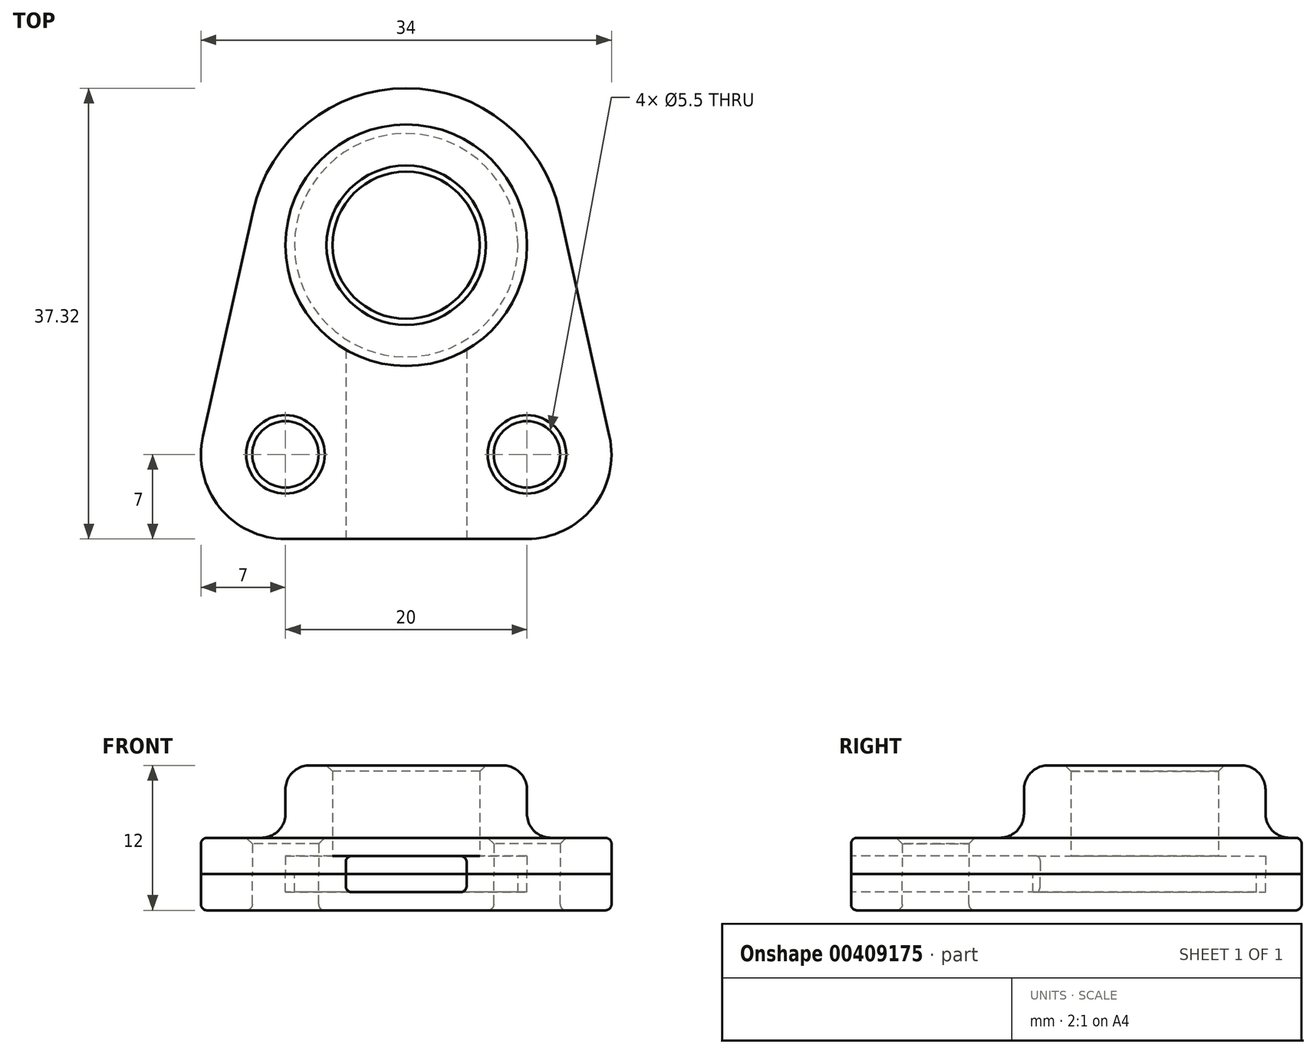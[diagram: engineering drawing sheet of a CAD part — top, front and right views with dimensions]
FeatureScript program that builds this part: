
annotation { "Feature Type Name" : "Feature", "Feature Type Description" : "" }
export const myFeature = defineFeature(function(context is Context, id is Id, definition is map)
    precondition{}
    {
        {
            var Q0;
            Q0=qCreatedBy(makeId("Top.planeOp"),FACE);
            var sketch = newSketch(context, id + "F0", { "sketchPlane" : qUnion([Q0])});
            skCircle(sketch, "E0", {"center": v(-20, 0) * mm, "radius": 2.75 * mm});
            skCircle(sketch, "E1", {"center": v(-10, 17.32) * mm, "radius": 10 * mm});
            skCircle(sketch, "E2", {"center": v(-10, 17.32) * mm, "radius": 6.1 * mm});
            skCircle(sketch, "E3", {"center": v(-10, 17.32) * mm, "radius": 5 * mm});
            skCircle(sketch, "E4", {"center": v(0, 0) * mm, "radius": 2.75 * mm});
            skLineSegment(sketch, "E5", {"start": v(-20, 0) * mm, "end": v(-10, 17.32) * mm, "construction": true});
            skLineSegment(sketch, "E6", {"start": v(-10, 17.32) * mm, "end": v(0, 0) * mm, "construction": true});
            skLineSegment(sketch, "E7", {"start": v(-20, 0) * mm, "end": v(0, 0) * mm, "construction": true});
            skArc(sketch, "E8", {"start": v(-26.83, 1.52) * mm, "mid": v(-25.46, -4.38) * mm, "end": v(-20, -7) * mm});
            skLineSegment(sketch, "E9", {"start": v(-27, 15.14) * mm, "end": v(-27, -13) * mm, "construction": true});
            skLineSegment(sketch, "E10", {"start": v(-10, 17.32) * mm, "end": v(-10, 0) * mm, "construction": true});
            skArc(sketch, "E11", {"start": v(2.69, 20.14) * mm, "mid": v(-10, 30.32) * mm, "end": v(-22.69, 20.14) * mm});
            skLineSegment(sketch, "E12", {"start": v(-22.69, 20.14) * mm, "end": v(-26.83, 1.52) * mm});
            skArc(sketch, "E13.MirrorC", {"start": v(6.83, 1.52) * mm, "mid": v(5.46, -4.38) * mm, "end": v(0, -7) * mm});
            skLineSegment(sketch, "E14.MirrorCS", {"start": v(2.69, 20.14) * mm, "end": v(6.83, 1.52) * mm});
            skLineSegment(sketch, "E15", {"start": v(-20, -7) * mm, "end": v(0, -7) * mm});
            skLineSegment(sketch, "E16", {"start": v(-15, 8.66) * mm, "end": v(-15, -7) * mm});
            skLineSegment(sketch, "E17.MirrorCS", {"start": v(-5, 8.66) * mm, "end": v(-5, -7) * mm});
            skCircle(sketch, "E18", {"center": v(-10, 17.32) * mm, "radius": 9.25 * mm});
            skSolve(sketch);
        }
        {
            var Q0;
            Q0=makeQuery(id+"F0.imprint","IMPRINT",FACE,{"disambiguationData":[TD([[makeQuery(id+"F0.imprint","IMPRINT",EDGE,{"derivedFrom":sQuery(id+"F0.wireOp",EDGE,"E0")}),-1.0]])]});
            var Q1;
            Q1=makeQuery(id+"F0.imprint","IMPRINT",FACE,{"disambiguationData":[TD([[makeQuery(id+"F0.imprint","IMPRINT",EDGE,{"derivedFrom":sQuery(id+"F0.wireOp",EDGE,"E1")}),1.0]])]});
            var Q2;
            {var subQ0=sQuery(id+"F0.wireOp",EDGE,"E16");Q2=makeQuery(id+"F0.imprint","IMPRINT",FACE,{"disambiguationData":[TD([[makeQuery(id+"F0.imprint","IMPRINT",EDGE,{"derivedFrom":subQ0}),1.0]])]});}
            extrude(context, id + "F1", {"entities" : qUnion([Q0, Q1, Q2]), "depth" : 3 * mm, "offsetDistance" : 25 * mm});
        }
        {
            var Q0;
            Q0=makeQuery(id+"F0.imprint","IMPRINT",FACE,{"disambiguationData":[TD([[makeQuery(id+"F0.imprint","IMPRINT",EDGE,{"derivedFrom":sQuery(id+"F0.wireOp",EDGE,"E1")}),1.0]])]});
            var Q1;
            Q1=makeQuery(id+"F0.imprint","IMPRINT",FACE,{"disambiguationData":[TD([[makeQuery(id+"F0.imprint","IMPRINT",EDGE,{"derivedFrom":sQuery(id+"F0.wireOp",EDGE,"E2")}),-1.0]])]});
            extrude(context, id + "F2", {"entities" : qUnion([Q0, Q1]), "operationType" : NewBodyOperationType.ADD, "depth" : 9 * mm});
        }
        {
            var Q0;
            Q0=makeQuery(id+"F0.imprint","IMPRINT",FACE,{"disambiguationData":[TD([[makeQuery(id+"F0.imprint","IMPRINT",EDGE,{"derivedFrom":sQuery(id+"F0.wireOp",EDGE,"E2")}),-1.0]])]});
            var Q1;
            {var subQ0=sQuery(id+"F0.wireOp",EDGE,"E16");Q1=makeQuery(id+"F0.imprint","IMPRINT",FACE,{"disambiguationData":[TD([[makeQuery(id+"F0.imprint","IMPRINT",EDGE,{"derivedFrom":subQ0}),1.0]])]});}
            var Q2;
            Q2=makeQuery(id+"F0.imprint","IMPRINT",FACE,{"disambiguationData":[TD([[makeQuery(id+"F0.imprint","IMPRINT",EDGE,{"derivedFrom":sQuery(id+"F0.wireOp",EDGE,"E18")}),-1.0]])]});
            extrude(context, id + "F3", {"entities" : qUnion([Q0, Q1, Q2]), "operationType" : NewBodyOperationType.REMOVE, "depth" : 1.5 * mm, "offsetDistance" : 25 * mm});
        }
        {
            var Q0;
            Q0=makeQuery(id+"F2.boolean.opBoolean","INTERSECT",EDGE,{"derivedFrom":[makeQuery(id+"F1.opExtrude","CAP_FACE",FACE,{"disambiguationData":[OSD([sQuery(id+"F0.wireOp",EDGE,"E0"),sQuery(id+"F0.wireOp",EDGE,"E2"),sQuery(id+"F0.wireOp",EDGE,"E4"),sQuery(id+"F0.wireOp",EDGE,"E8"),sQuery(id+"F0.wireOp",EDGE,"E11"),sQuery(id+"F0.wireOp",EDGE,"E12"),sQuery(id+"F0.wireOp",EDGE,"E13.MirrorC"),sQuery(id+"F0.wireOp",EDGE,"E14.MirrorCS"),sQuery(id+"F0.wireOp",EDGE,"E15")])],"isStart":false}),makeQuery(id+"F2.opExtrude","SWEPT_FACE",FACE,{"disambiguationData":[OSD([sQuery(id+"F0.wireOp",EDGE,"E1")])]})]});
            var Q1;
            Q1=makeQuery(id+"F2.opExtrude","CAP_EDGE",EDGE,{"disambiguationData":[OSD([sQuery(id+"F0.wireOp",EDGE,"E1")])],"isStart":false});
            fillet(context, id + "F4", {"entities" : qUnion([Q0, Q1]), "radius" : 2 * mm, "tangentPropagation" : true, "allowEdgeOverflow" : false});
        }
        {
            var Q0;
            Q0=makeQuery(id+"F2.opExtrude","CAP_EDGE",EDGE,{"disambiguationData":[OSD([sQuery(id+"F0.wireOp",EDGE,"E2")])],"isStart":false});
            var Q1;
            Q1=makeQuery(id+"F1.opExtrude","CAP_EDGE",EDGE,{"disambiguationData":[OSD([sQuery(id+"F0.wireOp",EDGE,"E0")])],"isStart":false});
            var Q2;
            Q2=makeQuery(id+"F1.opExtrude","CAP_EDGE",EDGE,{"disambiguationData":[OSD([sQuery(id+"F0.wireOp",EDGE,"E4")])],"isStart":false});
            chamfer(context, id + "F5", {"entities" : qUnion([Q0, Q1, Q2]), "width" : 0.5 * mm, "tangentPropagation" : true});
        }
        {
            var Q0;
            Q0=makeQuery(id+"F0.imprint","IMPRINT",FACE,{"disambiguationData":[TD([[makeQuery(id+"F0.imprint","IMPRINT",EDGE,{"derivedFrom":sQuery(id+"F0.wireOp",EDGE,"E0")}),-1.0]])]});
            var Q1;
            {var subQ0=sQuery(id+"F0.wireOp",EDGE,"E16");Q1=makeQuery(id+"F0.imprint","IMPRINT",FACE,{"disambiguationData":[TD([[makeQuery(id+"F0.imprint","IMPRINT",EDGE,{"derivedFrom":subQ0}),1.0]])]});}
            var Q2;
            Q2=makeQuery(id+"F0.imprint","IMPRINT",FACE,{"disambiguationData":[TD([[makeQuery(id+"F0.imprint","IMPRINT",EDGE,{"derivedFrom":sQuery(id+"F0.wireOp",EDGE,"E2")}),-1.0]])]});
            var Q3;
            Q3=makeQuery(id+"F0.imprint","IMPRINT",FACE,{"disambiguationData":[TD([[makeQuery(id+"F0.imprint","IMPRINT",EDGE,{"derivedFrom":sQuery(id+"F0.wireOp",EDGE,"E3")}),1.0]])]});
            var Q4;
            Q4=makeQuery(id+"F0.imprint","IMPRINT",FACE,{"disambiguationData":[TD([[makeQuery(id+"F0.imprint","IMPRINT",EDGE,{"derivedFrom":sQuery(id+"F0.wireOp",EDGE,"E2")}),1.0]])]});
            var Q5;
            Q5=makeQuery(id+"F0.imprint","IMPRINT",FACE,{"disambiguationData":[TD([[makeQuery(id+"F0.imprint","IMPRINT",EDGE,{"derivedFrom":sQuery(id+"F0.wireOp",EDGE,"E18")}),-1.0]])]});
            extrude(context, id + "F6", {"entities" : qUnion([Q0, Q1, Q2, Q3, Q4, Q5]), "oppositeDirection" : true, "depth" : 3 * mm, "offsetDistance" : 25 * mm});
        }
        {
            var Q0;
            {var subQ0=sQuery(id+"F0.wireOp",EDGE,"E16");Q0=makeQuery(id+"F0.imprint","IMPRINT",FACE,{"disambiguationData":[TD([[makeQuery(id+"F0.imprint","IMPRINT",EDGE,{"derivedFrom":subQ0}),1.0]])]});}
            var Q1;
            Q1=makeQuery(id+"F0.imprint","IMPRINT",FACE,{"disambiguationData":[TD([[makeQuery(id+"F0.imprint","IMPRINT",EDGE,{"derivedFrom":sQuery(id+"F0.wireOp",EDGE,"E18")}),-1.0]])]});
            extrude(context, id + "F7", {"entities" : qUnion([Q0, Q1]), "operationType" : NewBodyOperationType.REMOVE, "oppositeDirection" : true, "depth" : 1.5 * mm, "offsetDistance" : 25 * mm});
        }
        {
            var Q0;
            Q0=makeQuery(id+"F6.opExtrude","CAP_FACE",FACE,{"disambiguationData":[OSD([sQuery(id+"F0.wireOp",EDGE,"E0"),sQuery(id+"F0.wireOp",EDGE,"E4"),sQuery(id+"F0.wireOp",EDGE,"E8"),sQuery(id+"F0.wireOp",EDGE,"E11"),sQuery(id+"F0.wireOp",EDGE,"E12"),sQuery(id+"F0.wireOp",EDGE,"E13.MirrorC"),sQuery(id+"F0.wireOp",EDGE,"E14.MirrorCS"),sQuery(id+"F0.wireOp",EDGE,"E15")])],"isStart":false});
            var Q1;
            Q1=makeQuery(id+"F7.boolean.opBoolean","COPY",EDGE,{"derivedFrom":makeQuery(id+"F7.opExtrude","CAP_EDGE",EDGE,{"disambiguationData":[OSD([sQuery(id+"F0.wireOp",EDGE,"E16")])],"isStart":false})});
            var Q2;
            Q2=makeQuery(id+"F7.boolean.opBoolean","COPY",EDGE,{"derivedFrom":makeQuery(id+"F7.opExtrude","CAP_EDGE",EDGE,{"disambiguationData":[OSD([sQuery(id+"F0.wireOp",EDGE,"E17.MirrorCS")])],"isStart":false})});
            var Q3;
            Q3=makeQuery(id+"F3.boolean.opBoolean","COPY",EDGE,{"derivedFrom":makeQuery(id+"F3.opExtrude","CAP_EDGE",EDGE,{"disambiguationData":[OSD([sQuery(id+"F0.wireOp",EDGE,"E17.MirrorCS")])],"isStart":false})});
            var Q4;
            Q4=makeQuery(id+"F3.boolean.opBoolean","COPY",EDGE,{"derivedFrom":makeQuery(id+"F3.opExtrude","CAP_EDGE",EDGE,{"disambiguationData":[OSD([sQuery(id+"F0.wireOp",EDGE,"E16")])],"isStart":false})});
            var Q5;
            Q5=makeQuery(id+"F3.boolean.opBoolean","COPY",EDGE,{"derivedFrom":makeQuery(id+"F3.opExtrude","SWEPT_EDGE",EDGE,{"disambiguationData":[OSD([sQuery(id+"F0.wireOp",EDGE,"E15"),sQuery(id+"F0.wireOp",EDGE,"E16")])]})});
            var Q6;
            Q6=makeQuery(id+"F7.boolean.opBoolean","COPY",EDGE,{"derivedFrom":makeQuery(id+"F7.opExtrude","SWEPT_EDGE",EDGE,{"disambiguationData":[OSD([sQuery(id+"F0.wireOp",EDGE,"E15"),sQuery(id+"F0.wireOp",EDGE,"E16")])]})});
            var Q7;
            Q7=makeQuery(id+"F1.opExtrude","CAP_EDGE",EDGE,{"disambiguationData":[OSD([sQuery(id+"F0.wireOp",EDGE,"E8")])],"isStart":false});
            fillet(context, id + "F8", {"entities" : qUnion([Q0, Q1, Q2, Q3, Q4, Q5, Q6, Q7]), "radius" : 0.5 * mm, "tangentPropagation" : true, "allowEdgeOverflow" : false});
        }
    });
